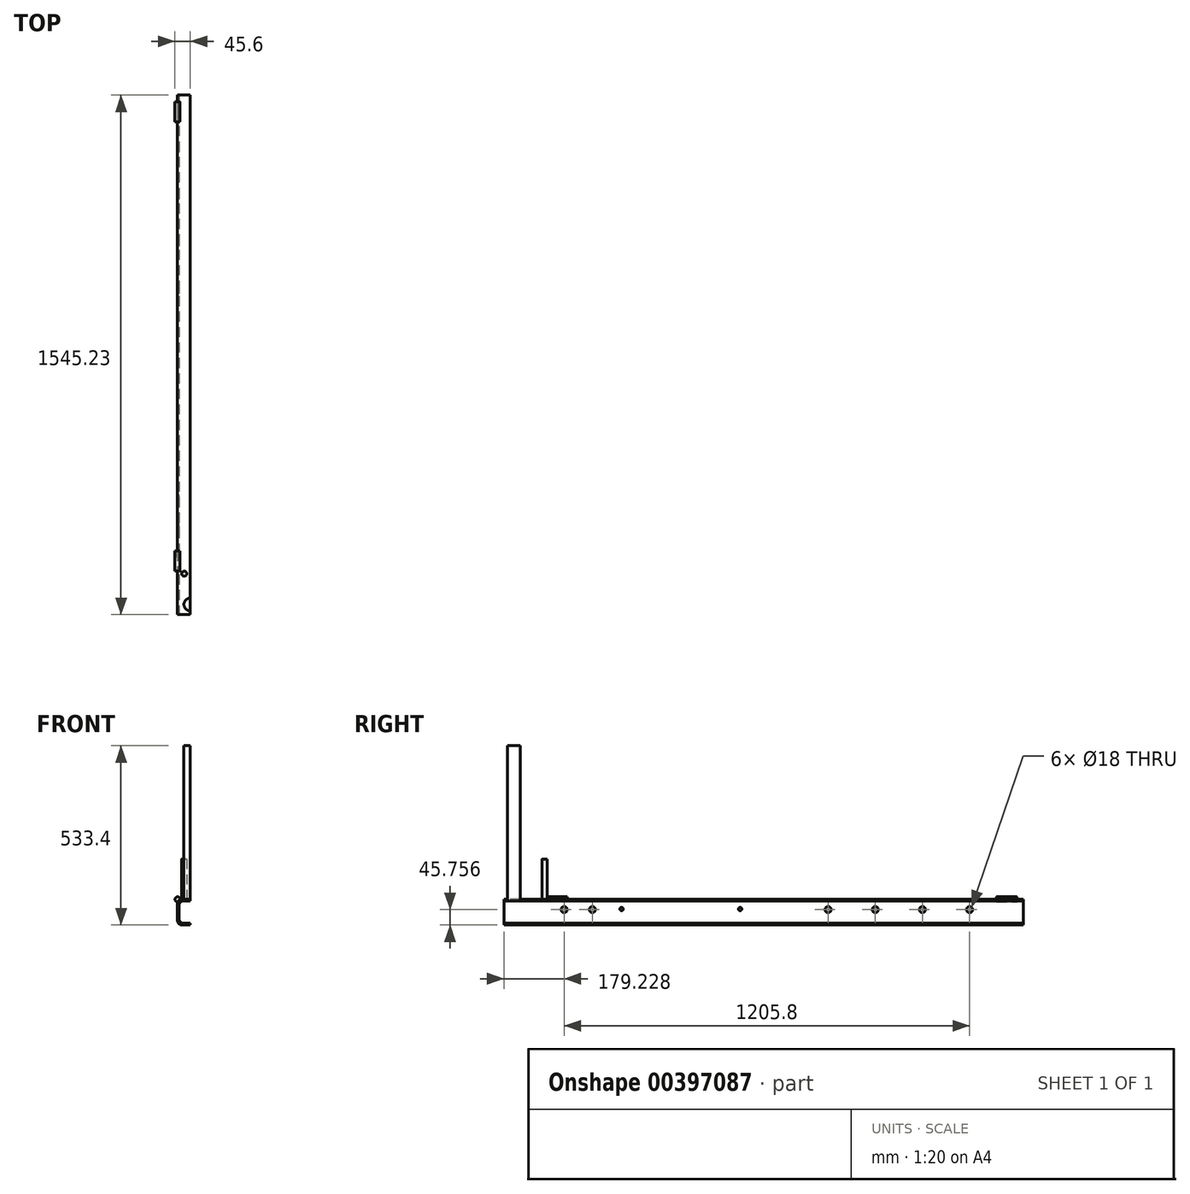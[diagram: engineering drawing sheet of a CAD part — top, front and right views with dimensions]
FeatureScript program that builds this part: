
annotation { "Feature Type Name" : "Feature", "Feature Type Description" : "" }
export const myFeature = defineFeature(function(context is Context, id is Id, definition is map)
    precondition{}
    {
        {
            var Q0;
            Q0=qCreatedBy(makeId("Front.planeOp"),FACE);
            var sketch = newSketch(context, id + "F0", { "sketchPlane" : qUnion([Q0])});
            skLineSegment(sketch, "E0.bottom", {"start": v(12.7, 0) * mm, "end": v(63.5, 0) * mm});
            skLineSegment(sketch, "E0.top", {"start": v(12.7, 76.2) * mm, "end": v(63.5, 76.2) * mm});
            skLineSegment(sketch, "E0.left", {"start": v(0, 12.7) * mm, "end": v(0, 63.5) * mm});
            skLineSegment(sketch, "E0.right", {"start": v(76.2, 12.7) * mm, "end": v(76.2, 63.5) * mm});
            skPoint(sketch, "E1.visualSharp", {"position": v(0, 76.2) * mm});
            skArc(sketch, "E1.filletArc", {"start": v(12.7, 76.2) * mm, "mid": v(3.72, 72.48) * mm, "end": v(0, 63.5) * mm});
            skPoint(sketch, "E2.visualSharp", {"position": v(76.2, 76.2) * mm});
            skArc(sketch, "E2.filletArc", {"start": v(76.2, 63.5) * mm, "mid": v(72.48, 72.48) * mm, "end": v(63.5, 76.2) * mm});
            skPoint(sketch, "E3.visualSharp", {"position": v(0, 0) * mm});
            skArc(sketch, "E3.filletArc", {"start": v(0, 12.7) * mm, "mid": v(3.72, 3.72) * mm, "end": v(12.7, 0) * mm});
            skPoint(sketch, "E4.visualSharp", {"position": v(76.2, 0) * mm});
            skArc(sketch, "E4.filletArc", {"start": v(63.5, 0) * mm, "mid": v(72.48, 3.72) * mm, "end": v(76.2, 12.7) * mm});
            skSolve(sketch);
        }
        {
            var Q0;
            Q0=qSketchRegion(id+"F0",true);
            extrude(context, id + "F1", {"entities" : qUnion([Q0]), "oppositeDirection" : true, "depth" : 1525.23 * mm});
        }
        {
            var Q0;
            Q0=makeQuery(id+"F1.opExtrude","CAP_FACE",FACE,{"disambiguationData":[OSD([sQuery(id+"F0.wireOp",EDGE,"E0.bottom"),sQuery(id+"F0.wireOp",EDGE,"E0.top"),sQuery(id+"F0.wireOp",EDGE,"E0.left"),sQuery(id+"F0.wireOp",EDGE,"E0.right"),sQuery(id+"F0.wireOp",EDGE,"E1.filletArc"),sQuery(id+"F0.wireOp",EDGE,"E2.filletArc"),sQuery(id+"F0.wireOp",EDGE,"E3.filletArc"),sQuery(id+"F0.wireOp",EDGE,"E4.filletArc")])],"isStart":true});
            var sketch = newSketch(context, id + "F2", { "sketchPlane" : qUnion([Q0])});
            skLineSegment(sketch, "E5", {"start": v(0, 38.1) * mm, "end": v(4.76, 38.1) * mm, "construction": true});
            skLineSegment(sketch, "E6", {"start": v(76.2, 38.1) * mm, "end": v(71.44, 38.1) * mm, "construction": true});
            skPoint(sketch, "E6.endSnap0", {"position": v(76.2, 38.1) * mm});
            skLineSegment(sketch, "E7", {"start": v(38.1, 76.2) * mm, "end": v(38.1, 71.44) * mm, "construction": true});
            skLineSegment(sketch, "E8", {"start": v(38.1, 0) * mm, "end": v(38.1, 4.76) * mm, "construction": true});
            skLineSegment(sketch, "E9", {"start": v(38.1, 4.76) * mm, "end": v(17.46, 4.76) * mm});
            skLineSegment(sketch, "E10", {"start": v(4.76, 17.46) * mm, "end": v(4.76, 58.74) * mm});
            skLineSegment(sketch, "E11", {"start": v(17.46, 71.44) * mm, "end": v(58.74, 71.44) * mm});
            skLineSegment(sketch, "E12", {"start": v(71.44, 58.74) * mm, "end": v(71.44, 17.46) * mm});
            skLineSegment(sketch, "E13", {"start": v(58.74, 4.76) * mm, "end": v(38.1, 4.76) * mm});
            skPoint(sketch, "E14.visualSharp", {"position": v(4.76, 71.44) * mm});
            skArc(sketch, "E14.filletArc", {"start": v(17.46, 71.44) * mm, "mid": v(8.48, 67.72) * mm, "end": v(4.76, 58.74) * mm});
            skPoint(sketch, "E15.visualSharp", {"position": v(71.44, 71.44) * mm});
            skArc(sketch, "E15.filletArc", {"start": v(71.44, 58.74) * mm, "mid": v(67.72, 67.72) * mm, "end": v(58.74, 71.44) * mm});
            skPoint(sketch, "E16.visualSharp", {"position": v(71.44, 4.76) * mm});
            skArc(sketch, "E16.filletArc", {"start": v(58.74, 4.76) * mm, "mid": v(67.72, 8.48) * mm, "end": v(71.44, 17.46) * mm});
            skPoint(sketch, "E17.visualSharp", {"position": v(4.76, 4.76) * mm});
            skArc(sketch, "E17.filletArc", {"start": v(4.76, 17.46) * mm, "mid": v(8.48, 8.48) * mm, "end": v(17.46, 4.76) * mm});
            skSolve(sketch);
        }
        {
            var Q0;
            Q0=makeQuery(id+"F2.imprint","IMPRINT",FACE,{"disambiguationData":[TD([[makeQuery(id+"F2.imprint","IMPRINT",EDGE,{"derivedFrom":sQuery(id+"F2.wireOp",EDGE,"E9")}),-1.0]])]});
            extrude(context, id + "F3", {"entities" : qUnion([Q0]), "operationType" : NewBodyOperationType.REMOVE, "oppositeDirection" : true, "depth" : 1525.23 * mm});
        }
        {
            var Q0;
            Q0=makeQuery(id+"F1.opExtrude","SWEPT_FACE",FACE,{"disambiguationData":[OSD([sQuery(id+"F0.wireOp",EDGE,"E0.right")])]});
            var sketch = newSketch(context, id + "F4", { "sketchPlane" : qUnion([Q0])});
            skLineSegment(sketch, "E18", {"start": v(1525.23, 63.5) * mm, "end": v(1525.23, 76.2) * mm, "construction": true});
            skLineSegment(sketch, "E19", {"start": v(1525.23, 76.2) * mm, "end": v(1525.23, 46.2) * mm, "construction": true});
            skLineSegment(sketch, "E20", {"start": v(1525.23, 46.2) * mm, "end": v(1335.23, 46.2) * mm, "construction": true});
            skLineSegment(sketch, "E21", {"start": v(1335.23, 46.2) * mm, "end": v(1105.03, 46.2) * mm, "construction": true});
            skLineSegment(sketch, "E22", {"start": v(1105.03, 46.2) * mm, "end": v(653.53, 46.2) * mm, "construction": true});
            skLineSegment(sketch, "E23", {"start": v(653.53, 46.2) * mm, "end": v(381.53, 46.2) * mm, "construction": true});
            skLineSegment(sketch, "E24", {"start": v(381.53, 46.2) * mm, "end": v(179.53, 46.2) * mm, "construction": true});
            skSolve(sketch);
        }
        {
            var Q0;
            Q0=sQuery(id+"F4.wireOp",VERTEX,"E21.start");
            var Q1;
            Q1=sQuery(id+"F4.wireOp",VERTEX,"E21.end");
            var Q2;
            Q2=sQuery(id+"F4.wireOp",VERTEX,"E23.start");
            var Q3;
            Q3=sQuery(id+"F4.wireOp",VERTEX,"E24.start");
            var Q4;
            Q4=sQuery(id+"F4.wireOp",VERTEX,"15NCYrLK-5f7F-d4hg-Meu1-zmrvhpbFYJVG.start");
            var Q5;
            Q5=sQuery(id+"F4.wireOp",VERTEX,"E24.end");
            var Q6;
            Q6=makeQuery(id+"F1.opExtrude","SWEPT_BODY",BODY,{"disambiguationData":[OSD([sQuery(id+"F0.wireOp",EDGE,"E0.bottom"),sQuery(id+"F0.wireOp",EDGE,"E0.top"),sQuery(id+"F0.wireOp",EDGE,"E0.left"),sQuery(id+"F0.wireOp",EDGE,"E0.right"),sQuery(id+"F0.wireOp",EDGE,"E1.filletArc"),sQuery(id+"F0.wireOp",EDGE,"E2.filletArc"),sQuery(id+"F0.wireOp",EDGE,"E3.filletArc"),sQuery(id+"F0.wireOp",EDGE,"E4.filletArc")])]});
            hole(context, id + "F5", {"style" : HoleStyle.SIMPLE, "endStyle" : HoleEndStyle.BLIND, "holeDiameter" : 19 * mm, "holeDepth" : 5 * mm, "isTappedThrough" : true, "tappedDepth" : 12 * mm, "tapClearance" : 3, "locations" : qUnion([Q0, Q1, Q2, Q3, Q4, Q5]), "scope" : qUnion([Q6])});
        }
        {
            var Q0;
            Q0=makeQuery(id+"F1.opExtrude","SWEPT_FACE",FACE,{"disambiguationData":[OSD([sQuery(id+"F0.wireOp",EDGE,"E0.right")])]});
            var sketch = newSketch(context, id + "F6", { "sketchPlane" : qUnion([Q0])});
            skLineSegment(sketch, "E25", {"start": v(1525.23, 63.5) * mm, "end": v(1525.23, 76.2) * mm});
            skLineSegment(sketch, "E26", {"start": v(1525.23, 76.2) * mm, "end": v(1525.23, 31.2) * mm, "construction": true});
            skLineSegment(sketch, "E27", {"start": v(1525.23, 31.2) * mm, "end": v(1442.06, 31.2) * mm, "construction": true});
            skLineSegment(sketch, "E28", {"start": v(1442.06, 31.2) * mm, "end": v(1218.7, 31.2) * mm, "construction": true});
            skLineSegment(sketch, "E29", {"start": v(1218.7, 31.2) * mm, "end": v(979.53, 31.2) * mm, "construction": true});
            skLineSegment(sketch, "E30", {"start": v(979.53, 31.2) * mm, "end": v(760.33, 31.2) * mm, "construction": true});
            skLineSegment(sketch, "E31", {"start": v(760.33, 31.2) * mm, "end": v(501.13, 31.2) * mm, "construction": true});
            skLineSegment(sketch, "E32", {"start": v(501.13, 31.2) * mm, "end": v(261.93, 31.2) * mm, "construction": true});
            skSolve(sketch);
        }
        {
            var Q0;
            Q0=sQuery(id+"F6.wireOp",VERTEX,"E32.end");
            var Q1;
            Q1=sQuery(id+"F6.wireOp",VERTEX,"E32.start");
            var Q2;
            Q2=sQuery(id+"F6.wireOp",VERTEX,"E31.start");
            var Q3;
            Q3=sQuery(id+"F6.wireOp",VERTEX,"E30.start");
            var Q4;
            Q4=sQuery(id+"F6.wireOp",VERTEX,"E28.end");
            var Q5;
            Q5=makeQuery(id+"F1.opExtrude","SWEPT_BODY",BODY,{"disambiguationData":[OSD([sQuery(id+"F0.wireOp",EDGE,"E0.bottom"),sQuery(id+"F0.wireOp",EDGE,"E0.top"),sQuery(id+"F0.wireOp",EDGE,"E0.left"),sQuery(id+"F0.wireOp",EDGE,"E0.right"),sQuery(id+"F0.wireOp",EDGE,"E1.filletArc"),sQuery(id+"F0.wireOp",EDGE,"E2.filletArc"),sQuery(id+"F0.wireOp",EDGE,"E3.filletArc"),sQuery(id+"F0.wireOp",EDGE,"E4.filletArc")])]});
            hole(context, id + "F7", {"style" : HoleStyle.SIMPLE, "endStyle" : HoleEndStyle.BLIND, "holeDiameter" : 9 * mm, "holeDepth" : 5 * mm, "isTappedThrough" : true, "tappedDepth" : 12 * mm, "tapClearance" : 3, "locations" : qUnion([Q0, Q1, Q2, Q3, Q4]), "scope" : qUnion([Q5])});
        }
        {
            var Q0;
            Q0=makeQuery(id+"F1.opExtrude","SWEPT_FACE",FACE,{"disambiguationData":[OSD([sQuery(id+"F0.wireOp",EDGE,"E0.top")])]});
            var sketch = newSketch(context, id + "F8", { "sketchPlane" : qUnion([Q0])});
            skLineSegment(sketch, "E33", {"start": v(38.1, 0) * mm, "end": v(38.1, 30) * mm, "construction": true});
            skCircle(sketch, "E34", {"center": v(38.1, 30) * mm, "radius": 19.05 * mm});
            skSolve(sketch);
        }
        {
            var Q0;
            Q0=makeQuery(id+"F8.imprint","IMPRINT",FACE,{"disambiguationData":[TD([[makeQuery(id+"F8.imprint","IMPRINT",EDGE,{"derivedFrom":sQuery(id+"F8.wireOp",EDGE,"E34")}),1.0]])]});
            extrude(context, id + "F9", {"entities" : qUnion([Q0]), "operationType" : NewBodyOperationType.ADD, "depth" : 457.2 * mm});
        }
        {
            var Q0;
            {var subQ0=sQuery(id+"F0.wireOp",EDGE,"E0.top");Q0=makeQuery(id+"FTddWvQlXHfw4Uw_1.boolean.opBoolean","MERGE",FACE,{"derivedFrom":[makeQuery(id+"F1.opExtrude","SWEPT_FACE",FACE,{"disambiguationData":[OSD([subQ0])]}),makeQuery(id+"FTddWvQlXHfw4Uw_1.opExtrude","SWEPT_FACE",FACE,{"disambiguationData":[OSD([subQ0])]})]});}
            var sketch = newSketch(context, id + "F10", { "sketchPlane" : qUnion([Q0])});
            skLineSegment(sketch, "E35", {"start": v(12.7, 0) * mm, "end": v(12.7, 30) * mm, "construction": true});
            skLineSegment(sketch, "E36", {"start": v(12.7, 30) * mm, "end": v(12.7, 49.05) * mm, "construction": true});
            skLineSegment(sketch, "E37", {"start": v(12.7, 49.05) * mm, "end": v(12.7, 121.55) * mm, "construction": true});
            skLineSegment(sketch, "E38", {"start": v(12.7, 121.55) * mm, "end": v(20.2, 121.55) * mm, "construction": true});
            skCircle(sketch, "E39", {"center": v(20.2, 121.55) * mm, "radius": 7.5 * mm});
            skSolve(sketch);
        }
        {
            var Q0;
            Q0=makeQuery(id+"F10.imprint","IMPRINT",FACE,{"disambiguationData":[TD([[makeQuery(id+"F10.imprint","IMPRINT",EDGE,{"derivedFrom":sQuery(id+"F10.wireOp",EDGE,"E39")}),1.0]])]});
            extrude(context, id + "F11", {"entities" : qUnion([Q0]), "operationType" : NewBodyOperationType.ADD, "depth" : 120 * mm});
        }
        {
            var Q0;
            Q0=makeQuery(id+"F1.opExtrude","CAP_FACE",FACE,{"disambiguationData":[OSD([sQuery(id+"F0.wireOp",EDGE,"E0.bottom"),sQuery(id+"F0.wireOp",EDGE,"E0.top"),sQuery(id+"F0.wireOp",EDGE,"E0.left"),sQuery(id+"F0.wireOp",EDGE,"E0.right"),sQuery(id+"F0.wireOp",EDGE,"E1.filletArc"),sQuery(id+"F0.wireOp",EDGE,"E2.filletArc"),sQuery(id+"F0.wireOp",EDGE,"E3.filletArc"),sQuery(id+"F0.wireOp",EDGE,"E4.filletArc")])],"isStart":false});
            extrude(context, id + "F12", {"entities" : qUnion([Q0]), "operationType" : NewBodyOperationType.ADD, "depth" : 20 * mm});
        }
        {
            var Q0;
            {var subQ0=sQuery(id+"F0.wireOp",EDGE,"E0.top");Q0=makeQuery(id+"F12.boolean.opBoolean","MERGE",FACE,{"derivedFrom":[makeQuery(id+"F1.opExtrude","SWEPT_FACE",FACE,{"disambiguationData":[OSD([subQ0])]}),makeQuery(id+"F12.opExtrude","SWEPT_FACE",FACE,{"disambiguationData":[OSD([subQ0])]})]});}
            var sketch = newSketch(context, id + "F13", { "sketchPlane" : qUnion([Q0])});
            skLineSegment(sketch, "E40", {"start": v(12.7, 121.55) * mm, "end": v(20.2, 121.55) * mm, "construction": true});
            skLineSegment(sketch, "E41", {"start": v(20.2, 121.55) * mm, "end": v(20.2, 129.05) * mm, "construction": true});
            skLineSegment(sketch, "E42", {"start": v(20.2, 129.05) * mm, "end": v(55.2, 129.05) * mm, "construction": true});
            skLineSegment(sketch, "E43", {"start": v(55.2, 129.05) * mm, "end": v(55.2, 0) * mm, "construction": true});
            skSolve(sketch);
        }
        {
            var Q0;
            {var subQ0=sQuery(id+"F0.wireOp",EDGE,"E0.right");Q0=makeQuery(id+"F12.boolean.opBoolean","MERGE",FACE,{"derivedFrom":[makeQuery(id+"F1.opExtrude","SWEPT_FACE",FACE,{"disambiguationData":[OSD([subQ0])]}),makeQuery(id+"F12.opExtrude","SWEPT_FACE",FACE,{"disambiguationData":[OSD([subQ0])]})]});}
            var sketch = newSketch(context, id + "F14", { "sketchPlane" : qUnion([Q0])});
            skLineSegment(sketch, "E44", {"start": v(0, 63.5) * mm, "end": v(129.05, 63.5) * mm, "construction": true});
            skSolve(sketch);
        }
        {
            var Q0;
            Q0=sQuery(id+"F13.wireOp",VERTEX,"E41.end");
            var Q1;
            Q1=sQuery(id+"F13.wireOp",VERTEX,"E42.end");
            var Q2;
            Q2=sQuery(id+"F14.wireOp",VERTEX,"E44.end");
            cPlane(context, id + "F15", {"entities" : qUnion([Q0, Q1, Q2]), "cplaneType" : CPlaneType.THREE_POINT, "offset" : 25 * mm, "width" : 150 * mm, "height" : 150 * mm});
        }
        {
            var Q0;
            Q0=qCreatedBy(id+"F15.planeOp",FACE);
            var sketch = newSketch(context, id + "F16", { "sketchPlane" : qUnion([Q0])});
            skLineSegment(sketch, "E45", {"start": v(0, 0) * mm, "end": v(0, 76.2) * mm, "construction": true});
            skCircle(sketch, "E46", {"center": v(0, 76.2) * mm, "radius": 7.5 * mm});
            skSolve(sketch);
        }
        {
            var Q0;
            Q0=qSketchRegion(id+"F16",true);
            extrude(context, id + "F17", {"entities" : qUnion([Q0]), "operationType" : NewBodyOperationType.ADD, "oppositeDirection" : true, "depth" : 60 * mm});
        }
        {
            var Q0;
            {var subQ6=sQuery(id+"F0.wireOp",EDGE,"E0.top");Q0=makeQuery(id+"F13.imprint","IMPRINT",FACE,{"disambiguationData":[TD([[makeQuery(id+"F13.imprint","IMPRINT",EDGE,{"derivedFrom":makeQuery(id+"F1.opExtrude","CAP_EDGE",EDGE,{"disambiguationData":[OSD([subQ6])],"isStart":true})}),1.0]])]});}
            var sketch = newSketch(context, id + "F18", { "sketchPlane" : qUnion([Q0])});
            skLineSegment(sketch, "E47", {"start": v(0, 0) * mm, "end": v(38.1, 0) * mm, "construction": true});
            skLineSegment(sketch, "E48", {"start": v(38.1, 0) * mm, "end": v(38.1, 1545.43) * mm, "construction": true});
            skSolve(sketch);
        }
        {
            var Q0;
            {var subQ6=sQuery(id+"F0.wireOp",EDGE,"E0.top");Q0=makeQuery(id+"F13.imprint","IMPRINT",FACE,{"disambiguationData":[TD([[makeQuery(id+"F13.imprint","IMPRINT",EDGE,{"derivedFrom":makeQuery(id+"F1.opExtrude","CAP_EDGE",EDGE,{"disambiguationData":[OSD([subQ6])],"isStart":true})}),1.0]])]});}
            var sketch = newSketch(context, id + "F19", { "sketchPlane" : qUnion([Q0])});
            skLineSegment(sketch, "E49", {"start": v(0, 0) * mm, "end": v(0, 1525.23) * mm, "construction": true});
            skLineSegment(sketch, "E50", {"start": v(0, 1525.23) * mm, "end": v(75.73, 1525.23) * mm, "construction": true});
            skSolve(sketch);
        }
        {
            var Q0;
            {var subQ0=sQuery(id+"F0.wireOp",EDGE,"E0.right");Q0=makeQuery(id+"F14.imprint","IMPRINT",FACE,{"disambiguationData":[TD([[makeQuery(id+"F14.imprint","IMPRINT",EDGE,{"derivedFrom":makeQuery(id+"F1.opExtrude","CAP_EDGE",EDGE,{"disambiguationData":[OSD([subQ0])],"isStart":true})}),-1.0]])]});}
            var sketch = newSketch(context, id + "F20", { "sketchPlane" : qUnion([Q0])});
            skLineSegment(sketch, "E51", {"start": v(0, 33.48) * mm, "end": v(1525.23, 33.48) * mm, "construction": true});
            skSolve(sketch);
        }
        {
            var Q0;
            Q0=sQuery(id+"F20.wireOp",VERTEX,"E51.end");
            var Q1;
            Q1=sQuery(id+"F19.wireOp",VERTEX,"E50.end");
            var Q2;
            Q2=sQuery(id+"F19.wireOp",VERTEX,"E49.end");
            cPlane(context, id + "F21", {"entities" : qUnion([Q0, Q1, Q2]), "cplaneType" : CPlaneType.THREE_POINT, "offset" : 25 * mm, "width" : 150 * mm, "height" : 150 * mm});
        }
        {
            var Q0;
            Q0=qCreatedBy(id+"F21.planeOp",FACE);
            var sketch = newSketch(context, id + "F22", { "sketchPlane" : qUnion([Q0])});
            skLineSegment(sketch, "E52", {"start": v(0, 0) * mm, "end": v(0, 76.2) * mm, "construction": true});
            skCircle(sketch, "E53", {"center": v(0, 76.2) * mm, "radius": 7.5 * mm});
            skSolve(sketch);
        }
        {
            var Q0;
            Q0=makeQuery(id+"F22.imprint","IMPRINT",FACE,{"disambiguationData":[TD([[makeQuery(id+"F22.imprint","IMPRINT",EDGE,{"derivedFrom":sQuery(id+"F22.wireOp",EDGE,"E53")}),1.0]])]});
            extrude(context, id + "F23", {"entities" : qUnion([Q0]), "operationType" : NewBodyOperationType.ADD, "oppositeDirection" : true, "depth" : 60 * mm});
        }
        {
            var Q0;
            Q0=makeQuery(id+"F12.opExtrude","CAP_EDGE",EDGE,{"disambiguationData":[OSD([sQuery(id+"F0.wireOp",EDGE,"E0.top")])],"isStart":false});
            cPoint(context, id + "F24", {"entities" : qUnion([Q0]), "parameter" : 0.5});
        }
        {
            var Q0;
            Q0=sQuery(id+"F18.wireOp",EDGE,"E48");
            cPoint(context, id + "F25", {"entities" : qUnion([Q0]), "parameter" : 0.5});
        }
        {
            var Q0;
            Q0=makeQuery(id+"F12.opExtrude","CAP_EDGE",EDGE,{"disambiguationData":[OSD([sQuery(id+"F0.wireOp",EDGE,"E0.bottom")])],"isStart":false});
            cPoint(context, id + "F26", {"entities" : qUnion([Q0]), "parameter" : 0.5});
        }
        {
            var Q0;
            Q0=qCreatedBy(id+"F24",VERTEX);
            var Q1;
            Q1=qCreatedBy(id+"F25",VERTEX);
            var Q2;
            Q2=qCreatedBy(id+"F26",VERTEX);
            cPlane(context, id + "F27", {"entities" : qUnion([Q0, Q1, Q2]), "cplaneType" : CPlaneType.THREE_POINT, "offset" : 25 * mm, "width" : 150 * mm, "height" : 150 * mm});
        }
        {
            var Q0;
            Q0=sQuery(id+"F6.wireOp",VERTEX,"E28.start");
            var Q1;
            Q1=makeQuery(id+"F1.opExtrude","SWEPT_BODY",BODY,{"disambiguationData":[OSD([sQuery(id+"F0.wireOp",EDGE,"E0.bottom"),sQuery(id+"F0.wireOp",EDGE,"E0.top"),sQuery(id+"F0.wireOp",EDGE,"E0.left"),sQuery(id+"F0.wireOp",EDGE,"E0.right"),sQuery(id+"F0.wireOp",EDGE,"E1.filletArc"),sQuery(id+"F0.wireOp",EDGE,"E2.filletArc"),sQuery(id+"F0.wireOp",EDGE,"E3.filletArc"),sQuery(id+"F0.wireOp",EDGE,"E4.filletArc")])]});
            hole(context, id + "F28", {"style" : HoleStyle.SIMPLE, "endStyle" : HoleEndStyle.BLIND, "holeDiameter" : 15 * mm, "holeDepth" : 5 * mm, "isTappedThrough" : true, "tappedDepth" : 12 * mm, "tapClearance" : 3, "locations" : qUnion([Q0]), "scope" : qUnion([Q1])});
        }
        {
            var Q0;
            {var subQ0=sQuery(id+"F0.wireOp",EDGE,"E0.left");Q0=makeQuery(id+"F12.boolean.opBoolean","MERGE",FACE,{"derivedFrom":[makeQuery(id+"F1.opExtrude","SWEPT_FACE",FACE,{"disambiguationData":[OSD([subQ0])]}),makeQuery(id+"F12.opExtrude","SWEPT_FACE",FACE,{"disambiguationData":[OSD([subQ0])]})]});}
            var sketch = newSketch(context, id + "F29", { "sketchPlane" : qUnion([Q0])});
            skLineSegment(sketch, "E54", {"start": v(0, 38.1) * mm, "end": v(0, 30.76) * mm, "construction": true});
            skLineSegment(sketch, "E55", {"start": v(0, 30.76) * mm, "end": v(0, 45.76) * mm, "construction": true});
            skLineSegment(sketch, "E56", {"start": v(-179.23, 45.76) * mm, "end": v(-263.44, 45.76) * mm, "construction": true});
            skLineSegment(sketch, "E57", {"start": v(-263.44, 45.76) * mm, "end": v(-964.43, 45.76) * mm, "construction": true});
            skLineSegment(sketch, "E58", {"start": v(-964.43, 45.76) * mm, "end": v(-1104.63, 45.76) * mm, "construction": true});
            skLineSegment(sketch, "E59", {"start": v(-1104.63, 45.76) * mm, "end": v(-1244.83, 45.76) * mm, "construction": true});
            skLineSegment(sketch, "E60", {"start": v(-1244.83, 45.76) * mm, "end": v(-1385.03, 45.76) * mm, "construction": true});
            skLineSegment(sketch, "E61", {"start": v(-1385.03, 45.76) * mm, "end": v(-1545.23, 45.76) * mm});
            skSolve(sketch);
        }
        {
            var Q0;
            Q0=sQuery(id+"F29.wireOp",VERTEX,"E60.end");
            var Q1;
            Q1=sQuery(id+"F29.wireOp",VERTEX,"E59.end");
            var Q2;
            Q2=sQuery(id+"F29.wireOp",VERTEX,"E59.start");
            var Q3;
            Q3=sQuery(id+"F29.wireOp",VERTEX,"E58.start");
            var Q4;
            Q4=sQuery(id+"F29.wireOp",VERTEX,"E57.start");
            var Q5;
            Q5=sQuery(id+"F29.wireOp",VERTEX,"E56.start");
            var Q6;
            Q6=makeQuery(id+"F1.opExtrude","SWEPT_BODY",BODY,{"disambiguationData":[OSD([sQuery(id+"F0.wireOp",EDGE,"E0.bottom"),sQuery(id+"F0.wireOp",EDGE,"E0.top"),sQuery(id+"F0.wireOp",EDGE,"E0.left"),sQuery(id+"F0.wireOp",EDGE,"E0.right"),sQuery(id+"F0.wireOp",EDGE,"E1.filletArc"),sQuery(id+"F0.wireOp",EDGE,"E2.filletArc"),sQuery(id+"F0.wireOp",EDGE,"E3.filletArc"),sQuery(id+"F0.wireOp",EDGE,"E4.filletArc")])]});
            hole(context, id + "F30", {"style" : HoleStyle.SIMPLE, "endStyle" : HoleEndStyle.BLIND, "holeDiameter" : 18 * mm, "holeDepth" : 5 * mm, "isTappedThrough" : true, "tappedDepth" : 12 * mm, "tapClearance" : 3, "locations" : qUnion([Q0, Q1, Q2, Q3, Q4, Q5]), "scope" : qUnion([Q6])});
        }
        {
            var Q0;
            {var subQ0=sQuery(id+"F0.wireOp",EDGE,"E0.left");Q0=makeQuery(id+"F12.boolean.opBoolean","MERGE",FACE,{"derivedFrom":[makeQuery(id+"F1.opExtrude","SWEPT_FACE",FACE,{"disambiguationData":[OSD([subQ0])]}),makeQuery(id+"F12.opExtrude","SWEPT_FACE",FACE,{"disambiguationData":[OSD([subQ0])]})]});}
            var sketch = newSketch(context, id + "F31", { "sketchPlane" : qUnion([Q0])});
            skLineSegment(sketch, "E62", {"start": v(-1545.23, 38.1) * mm, "end": v(-1545.23, 32.4) * mm, "construction": true});
            skLineSegment(sketch, "E63", {"start": v(-1545.23, 32.4) * mm, "end": v(-1545.23, 47.4) * mm, "construction": true});
            skLineSegment(sketch, "E64", {"start": v(-1545.23, 47.4) * mm, "end": v(-702.73, 47.4) * mm, "construction": true});
            skLineSegment(sketch, "E65", {"start": v(-702.73, 47.4) * mm, "end": v(-350.23, 47.4) * mm, "construction": true});
            skSolve(sketch);
        }
        {
            var Q0;
            Q0=sQuery(id+"F31.wireOp",VERTEX,"E65.start");
            var Q1;
            Q1=sQuery(id+"F31.wireOp",VERTEX,"E65.end");
            var Q2;
            Q2=makeQuery(id+"F1.opExtrude","SWEPT_BODY",BODY,{"disambiguationData":[OSD([sQuery(id+"F0.wireOp",EDGE,"E0.bottom"),sQuery(id+"F0.wireOp",EDGE,"E0.top"),sQuery(id+"F0.wireOp",EDGE,"E0.left"),sQuery(id+"F0.wireOp",EDGE,"E0.right"),sQuery(id+"F0.wireOp",EDGE,"E1.filletArc"),sQuery(id+"F0.wireOp",EDGE,"E2.filletArc"),sQuery(id+"F0.wireOp",EDGE,"E3.filletArc"),sQuery(id+"F0.wireOp",EDGE,"E4.filletArc")])]});
            hole(context, id + "F32", {"style" : HoleStyle.SIMPLE, "endStyle" : HoleEndStyle.BLIND, "holeDiameter" : 10 * mm, "holeDepth" : 5 * mm, "isTappedThrough" : true, "tappedDepth" : 12 * mm, "tapClearance" : 3, "locations" : qUnion([Q0, Q1]), "scope" : qUnion([Q2])});
        }
        {
            var Q0;
            {var subQ0=sQuery(id+"F0.wireOp",EDGE,"E0.bottom");Q0=makeQuery(id+"F12.boolean.opBoolean","MERGE",FACE,{"derivedFrom":[makeQuery(id+"F1.opExtrude","SWEPT_FACE",FACE,{"disambiguationData":[OSD([subQ0])]}),makeQuery(id+"F12.opExtrude","SWEPT_FACE",FACE,{"disambiguationData":[OSD([subQ0])]})]});}
            var sketch = newSketch(context, id + "F33", { "sketchPlane" : qUnion([Q0])});
            skLineSegment(sketch, "E66.bottom", {"start": v(38.1, 0) * mm, "end": v(113.1, 0) * mm});
            skLineSegment(sketch, "E66.top", {"start": v(38.1, -1545.23) * mm, "end": v(113.1, -1545.23) * mm});
            skLineSegment(sketch, "E66.left", {"start": v(38.1, 0) * mm, "end": v(38.1, -1545.23) * mm});
            skLineSegment(sketch, "E66.right", {"start": v(113.1, 0) * mm, "end": v(113.1, -1545.23) * mm});
            skSolve(sketch);
        }
        {
            var Q0;
            Q0=qSketchRegion(id+"F33",true);
            extrude(context, id + "F34", {"entities" : qUnion([Q0]), "operationType" : NewBodyOperationType.REMOVE, "oppositeDirection" : true, "depth" : 2500 * mm});
        }
    });
